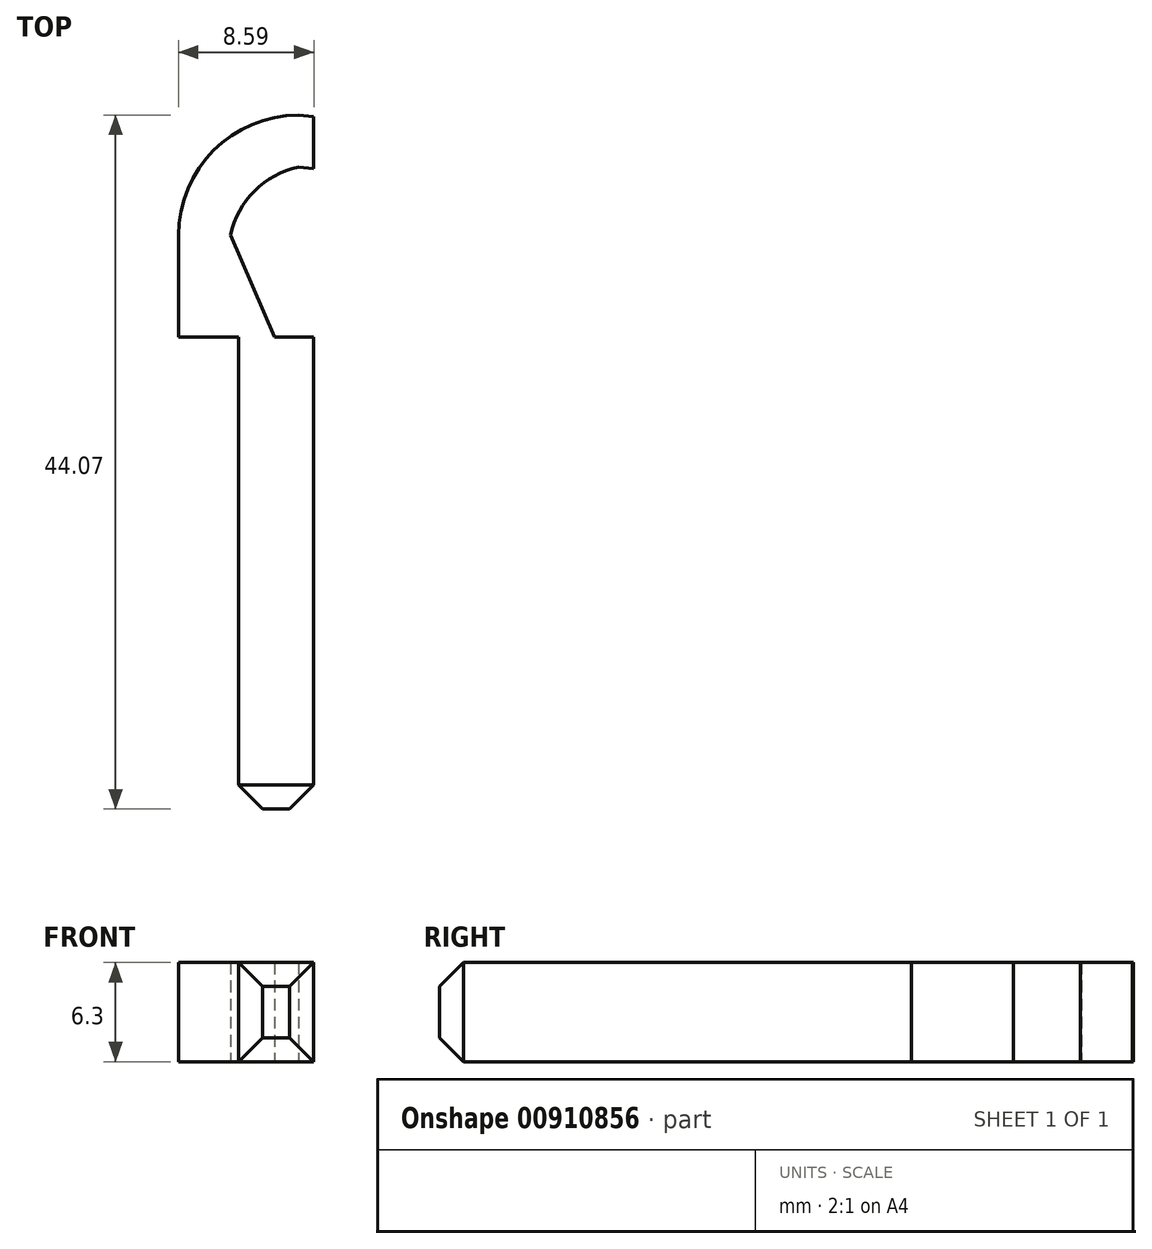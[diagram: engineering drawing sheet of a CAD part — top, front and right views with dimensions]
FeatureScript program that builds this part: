
annotation { "Feature Type Name" : "Feature", "Feature Type Description" : "" }
export const myFeature = defineFeature(function(context is Context, id is Id, definition is map)
    precondition{}
    {
        {
            var Q0;
            Q0=qCreatedBy(makeId("Top.planeOp"),FACE);
            var sketch = newSketch(context, id + "F0", { "sketchPlane" : qUnion([Q0])});
            skLineSegment(sketch, "E0.bottom", {"start": v(-2.02, -28.11) * mm, "end": v(1.8, -28.11) * mm});
            skLineSegment(sketch, "E0.left", {"start": v(-5.83, 1.86) * mm, "end": v(-5.83, 8.34) * mm});
            skArc(sketch, "E1", {"start": v(1.8, 15.96) * mm, "mid": v(-3.6, 13.73) * mm, "end": v(-5.83, 8.34) * mm});
            skArc(sketch, "E2", {"start": v(1.8, 12.66) * mm, "mid": v(-1, 11.14) * mm, "end": v(-2.53, 8.34) * mm});
            skLineSegment(sketch, "E3", {"start": v(1.8, 1.86) * mm, "end": v(0.27, 1.86) * mm});
            skLineSegment(sketch, "E4", {"start": v(-2.53, 8.34) * mm, "end": v(0.27, 1.86) * mm});
            skLineSegment(sketch, "E5", {"start": v(-5.83, 1.86) * mm, "end": v(-2.02, 1.86) * mm});
            skLineSegment(sketch, "E6", {"start": v(-2.02, 1.86) * mm, "end": v(-2.02, -28.11) * mm});
            skLineSegment(sketch, "E7", {"start": v(1.8, 1.86) * mm, "end": v(2.76, 1.86) * mm});
            skLineSegment(sketch, "E8", {"start": v(2.76, 1.86) * mm, "end": v(2.76, -28.11) * mm});
            skLineSegment(sketch, "E9", {"start": v(2.76, -28.11) * mm, "end": v(1.8, -28.11) * mm});
            skLineSegment(sketch, "E10", {"start": v(2.76, 12.57) * mm, "end": v(2.76, 15.88) * mm});
            skLineSegment(sketch, "E11", {"start": v(1.8, 12.66) * mm, "end": v(2.76, 12.57) * mm});
            skLineSegment(sketch, "E12", {"start": v(1.8, 15.96) * mm, "end": v(2.76, 15.88) * mm});
            skSolve(sketch);
        }
        {
            var Q0;
            Q0=makeQuery(id+"F0.imprint","IMPRINT",FACE,{"disambiguationData":[TD([[makeQuery(id+"F0.imprint","IMPRINT",EDGE,{"derivedFrom":sQuery(id+"F0.wireOp",EDGE,"E0.bottom")}),1.0]])]});
            extrude(context, id + "F1", {"entities" : qUnion([Q0]), "depth" : 6.3 * mm, "offsetDistance" : 25.4 * mm});
        }
        {
            var Q0;
            Q0=makeQuery(id+"F1.opExtrude","CAP_EDGE",EDGE,{"disambiguationData":[OSD([sQuery(id+"F0.wireOp",EDGE,"E0.bottom"),sQuery(id+"F0.wireOp",EDGE,"E9")])],"isStart":false});
            var Q1;
            Q1=makeQuery(id+"F1.opExtrude","SWEPT_EDGE",EDGE,{"disambiguationData":[OSD([sQuery(id+"F0.wireOp",EDGE,"E0.bottom"),sQuery(id+"F0.wireOp",EDGE,"E6")])]});
            var Q2;
            Q2=makeQuery(id+"F1.opExtrude","SWEPT_EDGE",EDGE,{"disambiguationData":[OSD([sQuery(id+"F0.wireOp",EDGE,"E8"),sQuery(id+"F0.wireOp",EDGE,"E9")])]});
            var Q3;
            Q3=makeQuery(id+"F1.opExtrude","CAP_EDGE",EDGE,{"disambiguationData":[OSD([sQuery(id+"F0.wireOp",EDGE,"E0.bottom"),sQuery(id+"F0.wireOp",EDGE,"E9")])],"isStart":true});
            chamfer(context, id + "F2", {"entities" : qUnion([Q0, Q1, Q2, Q3]), "width" : 1.52 * mm, "tangentPropagation" : true});
        }
    });
